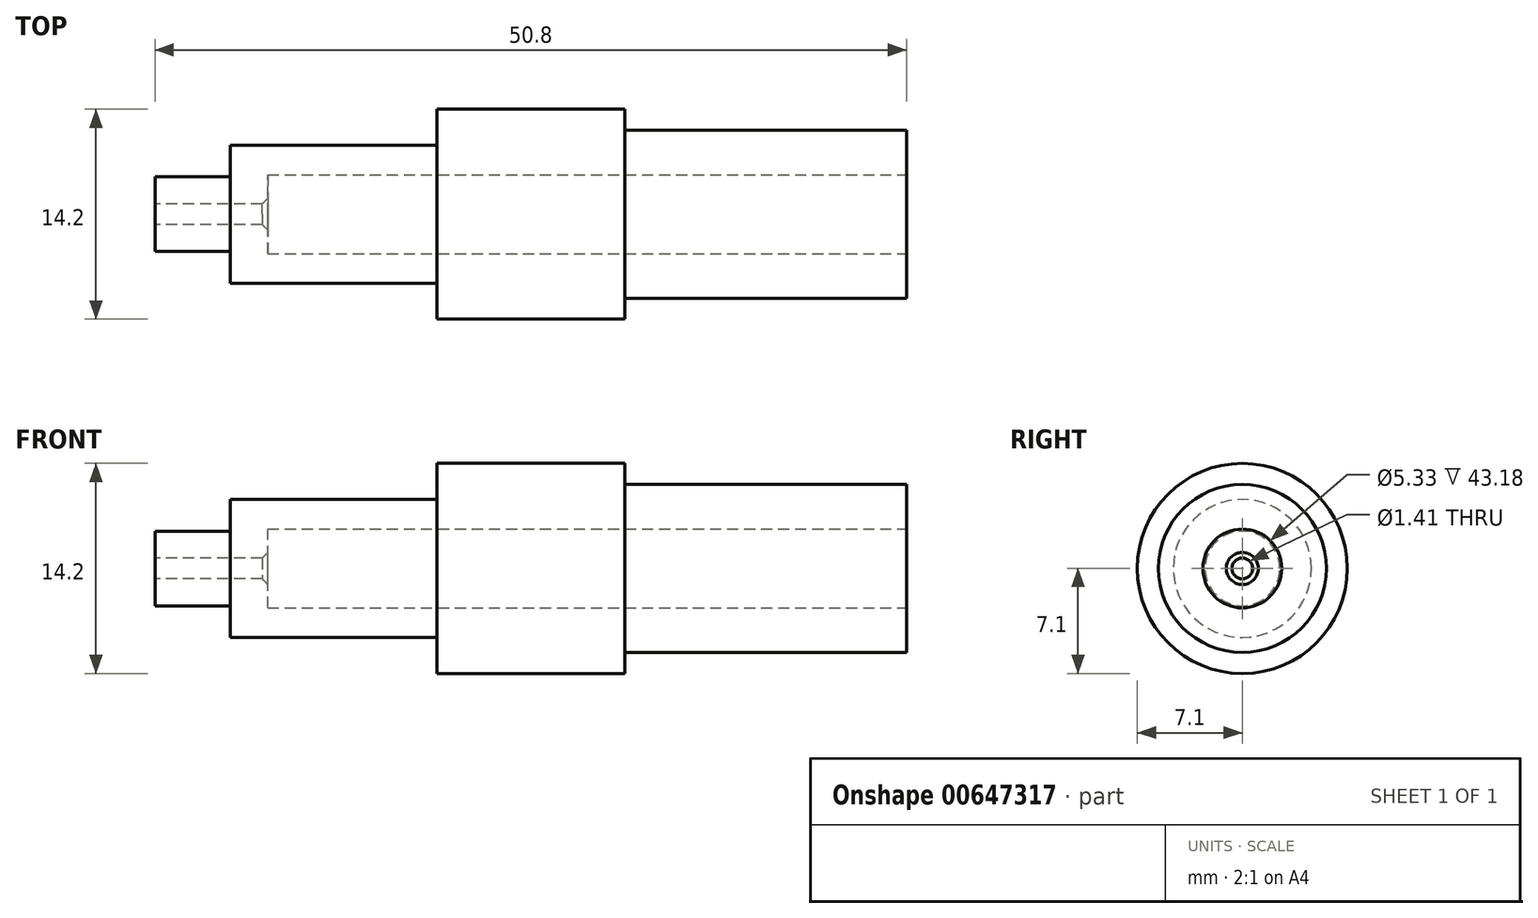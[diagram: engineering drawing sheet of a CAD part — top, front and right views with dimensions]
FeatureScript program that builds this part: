
annotation { "Feature Type Name" : "Feature", "Feature Type Description" : "" }
export const myFeature = defineFeature(function(context is Context, id is Id, definition is map)
    precondition{}
    {
        {
            var Q0;
            Q0=qCreatedBy(makeId("Right.planeOp"),FACE);
            var sketch = newSketch(context, id + "F0", { "sketchPlane" : qUnion([Q0])});
            skCircle(sketch, "E0", {"center": v(0, 0) * mm, "radius": 7.1 * mm});
            skSolve(sketch);
        }
        {
            var Q0;
            Q0=makeQuery(id+"F0.imprint","IMPRINT",FACE,{"disambiguationData":[TD([[makeQuery(id+"F0.imprint","IMPRINT",EDGE,{"derivedFrom":sQuery(id+"F0.wireOp",EDGE,"E0")}),1.0]])]});
            extrude(context, id + "F1", {"entities" : qUnion([Q0]), "depth" : 12.7 * mm, "offsetDistance" : 25.4 * mm});
        }
        {
            var Q0;
            Q0=makeQuery(id+"F1.opExtrude","CAP_FACE",FACE,{"disambiguationData":[OSD([sQuery(id+"F0.wireOp",EDGE,"E0")])],"isStart":false});
            var sketch = newSketch(context, id + "F2", { "sketchPlane" : qUnion([Q0])});
            skCircle(sketch, "E1", {"center": v(0, 0) * mm, "radius": 5.68 * mm});
            skSolve(sketch);
        }
        {
            var Q0;
            Q0=makeQuery(id+"F2.imprint","IMPRINT",FACE,{"disambiguationData":[TD([[makeQuery(id+"F2.imprint","IMPRINT",EDGE,{"derivedFrom":sQuery(id+"F2.wireOp",EDGE,"E1")}),1.0]])]});
            extrude(context, id + "F3", {"entities" : qUnion([Q0]), "operationType" : NewBodyOperationType.ADD, "depth" : 19.05 * mm, "offsetDistance" : 25.4 * mm});
        }
        {
            var Q0;
            Q0=makeQuery(id+"F1.opExtrude","CAP_FACE",FACE,{"disambiguationData":[OSD([sQuery(id+"F0.wireOp",EDGE,"E0")])],"isStart":true});
            var sketch = newSketch(context, id + "F4", { "sketchPlane" : qUnion([Q0])});
            skCircle(sketch, "E2", {"center": v(0, 0) * mm, "radius": 4.67 * mm});
            skSolve(sketch);
        }
        {
            var Q0;
            Q0=makeQuery(id+"F4.imprint","IMPRINT",FACE,{"disambiguationData":[TD([[makeQuery(id+"F4.imprint","IMPRINT",EDGE,{"derivedFrom":sQuery(id+"F4.wireOp",EDGE,"E2")}),1.0]])]});
            extrude(context, id + "F5", {"entities" : qUnion([Q0]), "operationType" : NewBodyOperationType.ADD, "depth" : 13.97 * mm, "offsetDistance" : 25.4 * mm});
        }
        {
            var Q0;
            Q0=makeQuery(id+"F5.opExtrude","CAP_FACE",FACE,{"disambiguationData":[OSD([sQuery(id+"F4.wireOp",EDGE,"E2")])],"isStart":false});
            var sketch = newSketch(context, id + "F6", { "sketchPlane" : qUnion([Q0])});
            skCircle(sketch, "E3", {"center": v(0, 0) * mm, "radius": 2.52 * mm});
            skSolve(sketch);
        }
        {
            var Q0;
            Q0=makeQuery(id+"F6.imprint","IMPRINT",FACE,{"disambiguationData":[TD([[makeQuery(id+"F6.imprint","IMPRINT",EDGE,{"derivedFrom":sQuery(id+"F6.wireOp",EDGE,"E3")}),1.0]])]});
            extrude(context, id + "F7", {"entities" : qUnion([Q0]), "operationType" : NewBodyOperationType.ADD, "depth" : 5.08 * mm, "offsetDistance" : 25.4 * mm});
        }
        {
            var Q0;
            Q0=makeQuery(id+"F3.opExtrude","CAP_FACE",FACE,{"disambiguationData":[OSD([sQuery(id+"F2.wireOp",EDGE,"E1")])],"isStart":false});
            var sketch = newSketch(context, id + "F8", { "sketchPlane" : qUnion([Q0])});
            skCircle(sketch, "E4", {"center": v(0, 0) * mm, "radius": 2.67 * mm});
            skSolve(sketch);
        }
        {
            var Q0;
            Q0=makeQuery(id+"F8.imprint","IMPRINT",FACE,{"disambiguationData":[TD([[makeQuery(id+"F8.imprint","IMPRINT",EDGE,{"derivedFrom":sQuery(id+"F8.wireOp",EDGE,"E4")}),1.0]])]});
            extrude(context, id + "F9", {"entities" : qUnion([Q0]), "operationType" : NewBodyOperationType.REMOVE, "oppositeDirection" : true, "depth" : 43.18 * mm, "offsetDistance" : 25.4 * mm});
        }
        {
            var Q0;
            Q0=makeQuery(id+"F7.opExtrude","CAP_FACE",FACE,{"disambiguationData":[OSD([sQuery(id+"F6.wireOp",EDGE,"E3")])],"isStart":false});
            var sketch = newSketch(context, id + "F10", { "sketchPlane" : qUnion([Q0])});
            skCircle(sketch, "E5", {"center": v(0, 0) * mm, "radius": 0.7 * mm});
            skSolve(sketch);
        }
        {
            var Q0;
            Q0=makeQuery(id+"F10.imprint","IMPRINT",FACE,{"disambiguationData":[TD([[makeQuery(id+"F10.imprint","IMPRINT",EDGE,{"derivedFrom":sQuery(id+"F10.wireOp",EDGE,"E5")}),1.0]])]});
            extrude(context, id + "F11", {"entities" : qUnion([Q0]), "operationType" : NewBodyOperationType.REMOVE, "oppositeDirection" : true, "depth" : 25.4 * mm, "offsetDistance" : 25.4 * mm});
        }
        {
            var Q0;
            Q0=makeQuery(id+"F11.boolean.opBoolean","INTERSECT",EDGE,{"derivedFrom":[makeQuery(id+"F9.boolean.opBoolean","COPY",FACE,{"derivedFrom":makeQuery(id+"F9.opExtrude","CAP_FACE",FACE,{"disambiguationData":[OSD([sQuery(id+"F8.wireOp",EDGE,"E4")])],"isStart":false})}),makeQuery(id+"F11.opExtrude","SWEPT_FACE",FACE,{"disambiguationData":[OSD([sQuery(id+"F10.wireOp",EDGE,"E5")])]})]});
            chamfer(context, id + "F12", {"entities" : qUnion([Q0]), "width" : 0.38 * mm, "tangentPropagation" : true});
        }
        {
            var Q0;
            Q0=qCreatedBy(makeId("Top.planeOp"),FACE);
            var sketch = newSketch(context, id + "F13", { "sketchPlane" : qUnion([Q0])});
            skLineSegment(sketch, "E6", {"start": v(0, 7.1) * mm, "end": v(12.7, 7.1) * mm});
            skLineSegment(sketch, "E7", {"start": v(12.7, -7.1) * mm, "end": v(0, -7.1) * mm});
            skCircle(sketch, "E8", {"center": v(5.08, 0) * mm, "radius": 3.81 * mm});
            skSolve(sketch);
        }
        {
            var Q0;
            Q0=sQuery(id+"F13.wireOp",EDGE,"E8");
            extrude(context, id + "F14", {"bodyType" : ToolBodyType.SURFACE, "surfaceEntities" : qUnion([Q0]), "depth" : 7.62 * mm, "offsetDistance" : 25.4 * mm});
        }
    });
